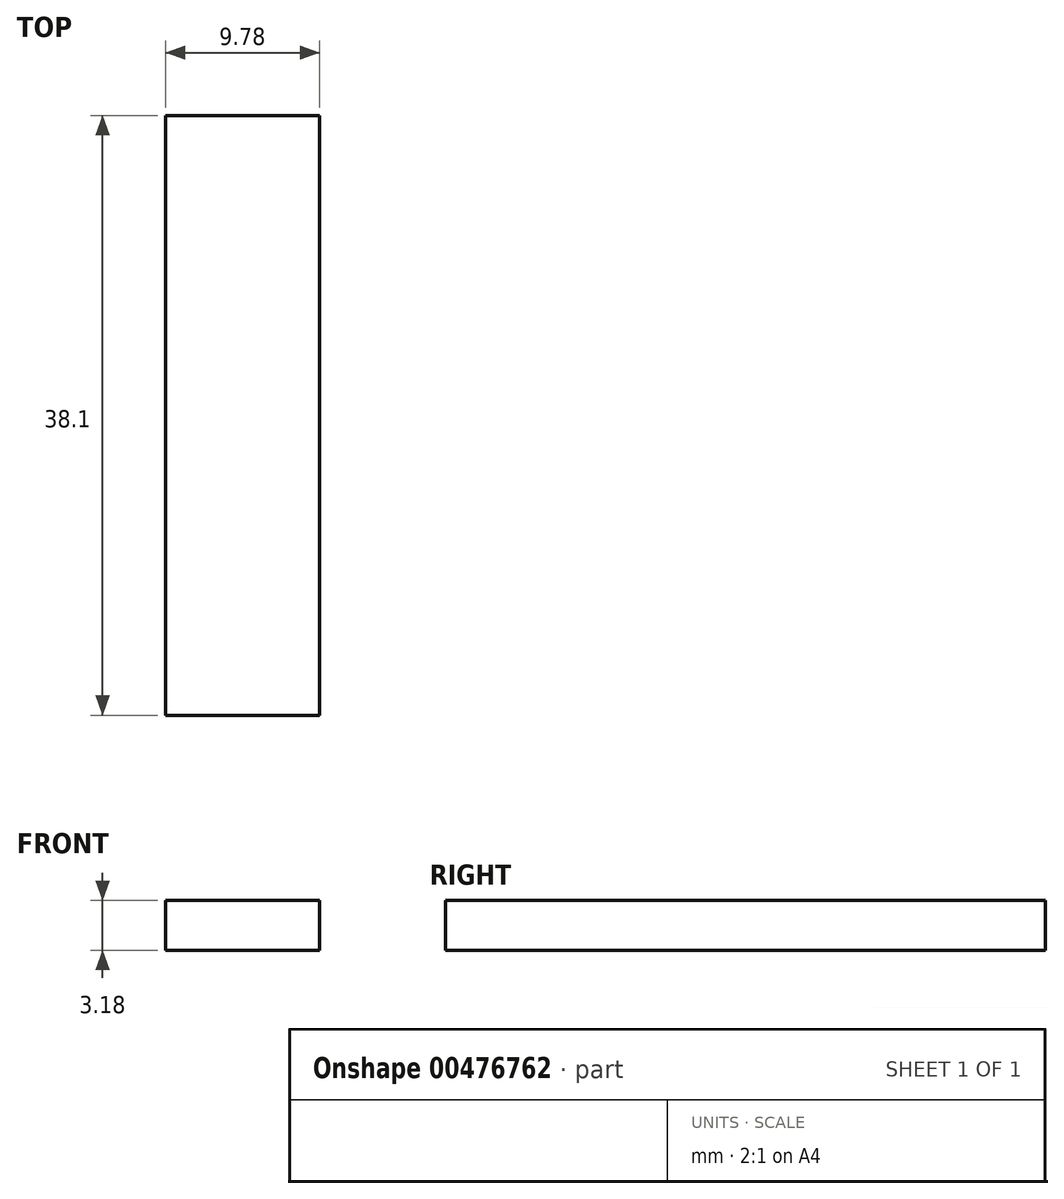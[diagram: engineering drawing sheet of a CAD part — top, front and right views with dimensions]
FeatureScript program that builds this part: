
annotation { "Feature Type Name" : "Feature", "Feature Type Description" : "" }
export const myFeature = defineFeature(function(context is Context, id is Id, definition is map)
    precondition{}
    {
        {
            var Q0;
            Q0=qCreatedBy(makeId("Right.planeOp"),FACE);
            var sketch = newSketch(context, id + "F0", { "sketchPlane" : qUnion([Q0])});
            skLineSegment(sketch, "E0.bottom", {"start": v(19.05, -1.59) * mm, "end": v(-19.05, -1.59) * mm});
            skLineSegment(sketch, "E0.top", {"start": v(19.05, 1.59) * mm, "end": v(-19.05, 1.59) * mm});
            skLineSegment(sketch, "E0.left", {"start": v(19.05, -1.59) * mm, "end": v(19.05, 1.59) * mm});
            skLineSegment(sketch, "E0.right", {"start": v(-19.05, -1.59) * mm, "end": v(-19.05, 1.59) * mm});
            skPoint(sketch, "E0.middle", {"position": v(0, 0) * mm});
            skSolve(sketch);
        }
        {
            var Q0;
            Q0=makeQuery(id+"F0.imprint","IMPRINT",FACE,{"disambiguationData":[TD([[makeQuery(id+"F0.imprint","IMPRINT",EDGE,{"derivedFrom":sQuery(id+"F0.wireOp",EDGE,"E0.bottom")}),-1.0]])]});
            extrude(context, id + "F1", {"entities" : qUnion([Q0]), "depth" : 9.78 * mm, "symmetric" : true});
        }
    });
